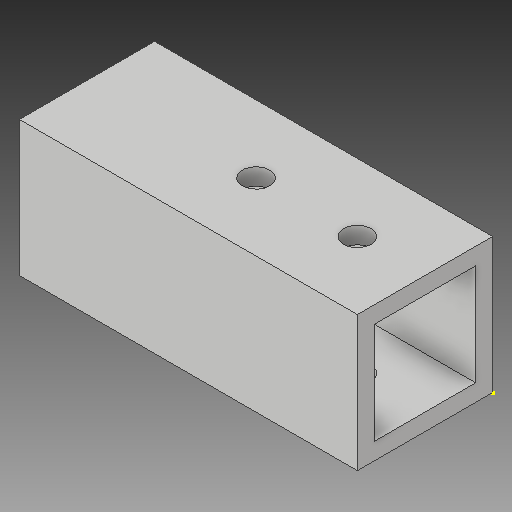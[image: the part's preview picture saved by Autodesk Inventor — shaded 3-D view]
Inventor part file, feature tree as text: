
AUTODESK INVENTOR PART (.ipt)
format: ipt  version: 2018 (Build 220112000, 112)  size: 108,032 bytes
history: native  units: in
note: dims shown in document units (in); Inventor stores cm internally (conversion verified against a paired STEP export)
features: sketch x4, other x3
ambient origin geometry x8: Origin, YZ Plane, XZ Plane, XY Plane, X Axis, Y Axis, Z Axis, Center Point
bodies: Solid1 (feature_tree)
feature tree (7):
  other  "wheel tip connector 1.ipt"
  other  "Solid1::wheel tip connector 1.ipt"
  other  "TaggingFeature1"
  sketch  "Sketch1"  dims[d0=0.3937in]
  sketch  "Sketch2"
  sketch  "Sketch3"
  sketch  "Sketch4"
